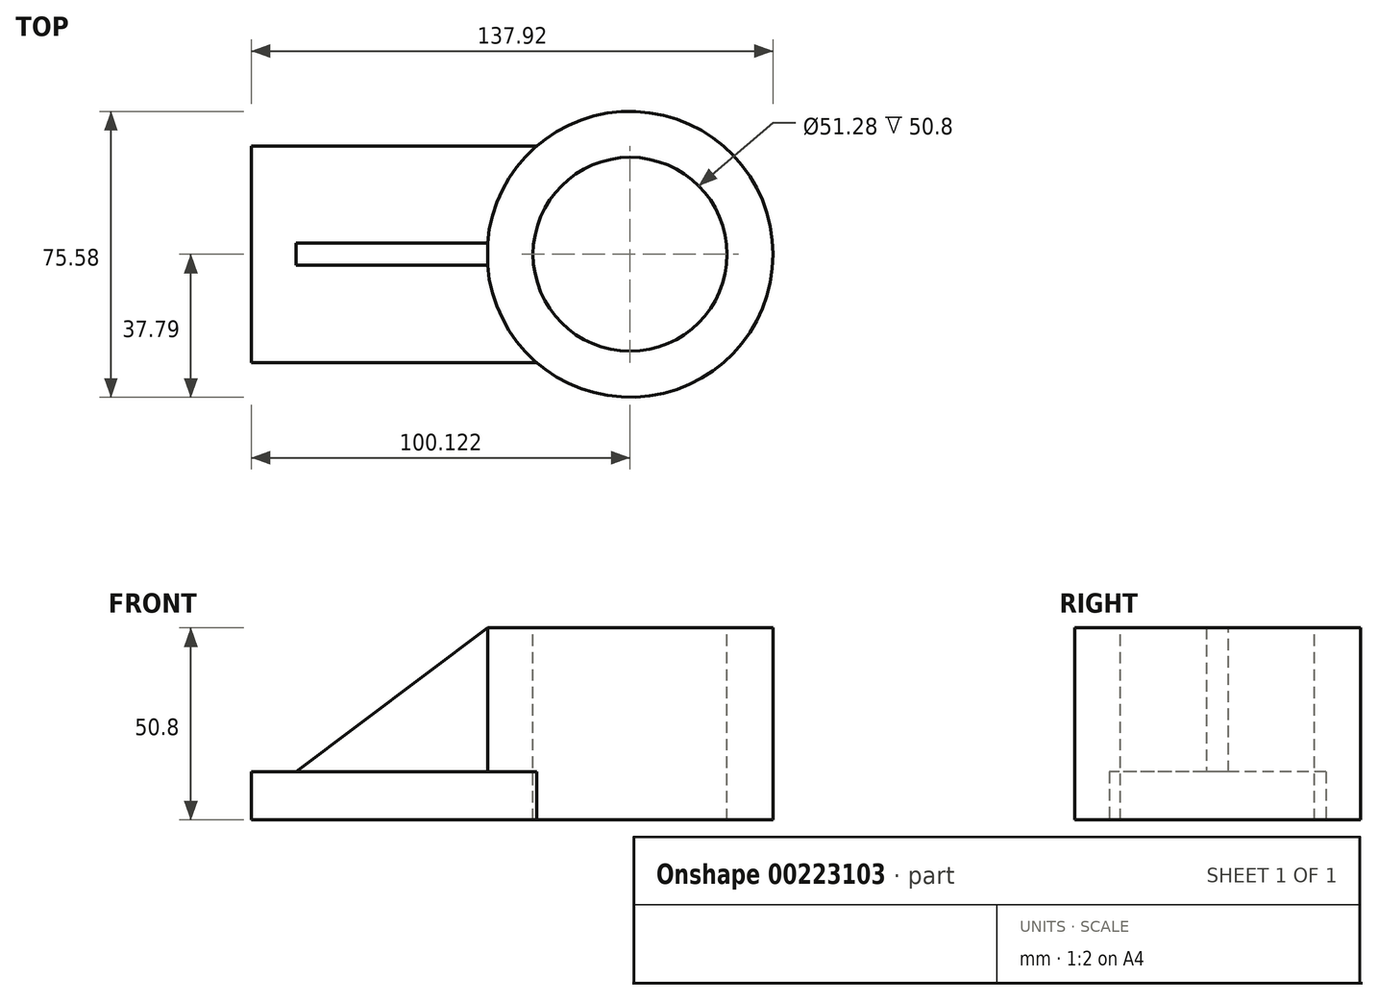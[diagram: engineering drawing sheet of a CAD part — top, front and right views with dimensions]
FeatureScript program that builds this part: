
annotation { "Feature Type Name" : "Feature", "Feature Type Description" : "" }
export const myFeature = defineFeature(function(context is Context, id is Id, definition is map)
    precondition{}
    {
        {
            var Q0;
            Q0=qCreatedBy(makeId("Top.planeOp"),FACE);
            var sketch = newSketch(context, id + "F0", { "sketchPlane" : qUnion([Q0])});
            skLineSegment(sketch, "E0.bottom", {"start": v(61.9, 28.67) * mm, "end": v(-61.9, 28.67) * mm});
            skLineSegment(sketch, "E0.top", {"start": v(61.9, -28.67) * mm, "end": v(-61.9, -28.67) * mm});
            skLineSegment(sketch, "E0.left", {"start": v(61.9, 28.67) * mm, "end": v(61.9, -28.67) * mm});
            skLineSegment(sketch, "E0.right", {"start": v(-61.9, 28.67) * mm, "end": v(-61.9, -28.67) * mm});
            skPoint(sketch, "E0.middle", {"position": v(0, 0) * mm});
            skSolve(sketch);
        }
        {
            var Q0;
            Q0 = qSketchRegion(id + "F0", true);
            extrude(context, id + "F1", {"entities" : qUnion([Q0]), "depth" : 12.7 * mm});
        }
        {
            var Q0;
            Q0=qCreatedBy(makeId("Top.planeOp"),FACE);
            var sketch = newSketch(context, id + "F2", { "sketchPlane" : qUnion([Q0])});
            skCircle(sketch, "E1", {"center": v(38.22, 0) * mm, "radius": 37.8 * mm});
            skSolve(sketch);
        }
        {
            var Q0;
            Q0 = qSketchRegion(id + "F2", true);
            extrude(context, id + "F3", {"entities" : qUnion([Q0]), "operationType" : NewBodyOperationType.ADD, "depth" : 50.8 * mm});
        }
        {
            var Q0;
            Q0=makeQuery(id+"F3.opExtrude","CAP_FACE",FACE,{"disambiguationData":[OSD([sQuery(id+"F2.wireOp",EDGE,"E1")])],"isStart":false});
            var sketch = newSketch(context, id + "F4", { "sketchPlane" : qUnion([Q0])});
            skCircle(sketch, "E2", {"center": v(38.22, 0) * mm, "radius": 25.64 * mm});
            skSolve(sketch);
        }
        {
            var Q0;
            Q0 = qSketchRegion(id + "F4", true);
            extrude(context, id + "F5", {"entities" : qUnion([Q0]), "operationType" : NewBodyOperationType.REMOVE, "oppositeDirection" : true, "depth" : 50.8 * mm});
        }
        {
            var Q0;
            Q0=makeQuery(id+"F1.opExtrude","CAP_FACE",FACE,{"disambiguationData":[OSD([sQuery(id+"F0.wireOp",EDGE,"E0.bottom"),sQuery(id+"F0.wireOp",EDGE,"E0.top"),sQuery(id+"F0.wireOp",EDGE,"E0.left"),sQuery(id+"F0.wireOp",EDGE,"E0.right")])],"isStart":false});
            var sketch = newSketch(context, id + "F6", { "sketchPlane" : qUnion([Q0])});
            skLineSegment(sketch, "E3.bottom", {"start": v(-50.14, 2.92) * mm, "end": v(50.14, 2.92) * mm});
            skLineSegment(sketch, "E3.top", {"start": v(-50.14, -2.92) * mm, "end": v(50.14, -2.92) * mm});
            skLineSegment(sketch, "E3.left", {"start": v(-50.14, 2.92) * mm, "end": v(-50.14, -2.92) * mm});
            skLineSegment(sketch, "E3.right", {"start": v(50.14, 2.92) * mm, "end": v(50.14, -2.92) * mm});
            skPoint(sketch, "E3.middle", {"position": v(0, 0) * mm});
            skSolve(sketch);
        }
        {
            var Q0;
            Q0 = qSketchRegion(id + "F6", true);
            extrude(context, id + "F7", {"entities" : qUnion([Q0]), "operationType" : NewBodyOperationType.ADD, "depth" : 38.1 * mm});
        }
        {
            var Q0;
            Q0=makeQuery(id+"F7.boolean.opBoolean","MERGE",FACE,{"derivedFrom":[makeQuery(id+"F3.opExtrude","CAP_FACE",FACE,{"disambiguationData":[OSD([sQuery(id+"F2.wireOp",EDGE,"E1")])],"isStart":false}),makeQuery(id+"F7.opExtrude","CAP_FACE",FACE,{"disambiguationData":[OSD([sQuery(id+"F6.wireOp",EDGE,"E3.bottom"),sQuery(id+"F6.wireOp",EDGE,"E3.top"),sQuery(id+"F6.wireOp",EDGE,"E3.left"),sQuery(id+"F6.wireOp",EDGE,"E3.right")])],"isStart":false})]});
            var sketch = newSketch(context, id + "F8", { "sketchPlane" : qUnion([Q0])});
            skCircle(sketch, "E4", {"center": v(38.22, 0) * mm, "radius": 25.64 * mm});
            skSolve(sketch);
        }
        {
            var Q0;
            Q0 = qSketchRegion(id + "F8", true);
            extrude(context, id + "F9", {"entities" : qUnion([Q0]), "operationType" : NewBodyOperationType.REMOVE, "oppositeDirection" : true, "depth" : 50.8 * mm});
        }
        {
            var Q0;
            {var subQ1=sQuery(id+"F6.wireOp",EDGE,"E3.top");var subQ2=sQuery(id+"F2.wireOp",EDGE,"E1");Q0=makeQuery(id+"F7.boolean.opBoolean","SPLIT",FACE,{"disambiguationData":[TD([makeQuery(id+"F3.opExtrude","SWEPT_FACE",FACE,{"disambiguationData":[OSD([subQ2])]})])],"derivedFrom":makeQuery(id+"F7.opExtrude","SWEPT_FACE",FACE,{"disambiguationData":[OSD([subQ1])]})});}
            var sketch = newSketch(context, id + "F10", { "sketchPlane" : qUnion([Q0])});
            skLineSegment(sketch, "E5", {"start": v(0.54, 50.8) * mm, "end": v(-50.14, 12.7) * mm});
            skSolve(sketch);
        }
        {
            var Q0;
            Q0=makeQuery(id+"F10.imprint","IMPRINT",FACE,{"disambiguationData":[TD([[makeQuery(id+"F10.imprint","IMPRINT",EDGE,{"derivedFrom":sQuery(id+"F10.wireOp",EDGE,"E5")}),-1.0]])]});
            extrude(context, id + "F11", {"entities" : qUnion([Q0]), "operationType" : NewBodyOperationType.REMOVE, "oppositeDirection" : true, "depth" : 25.4 * mm});
        }
    });
